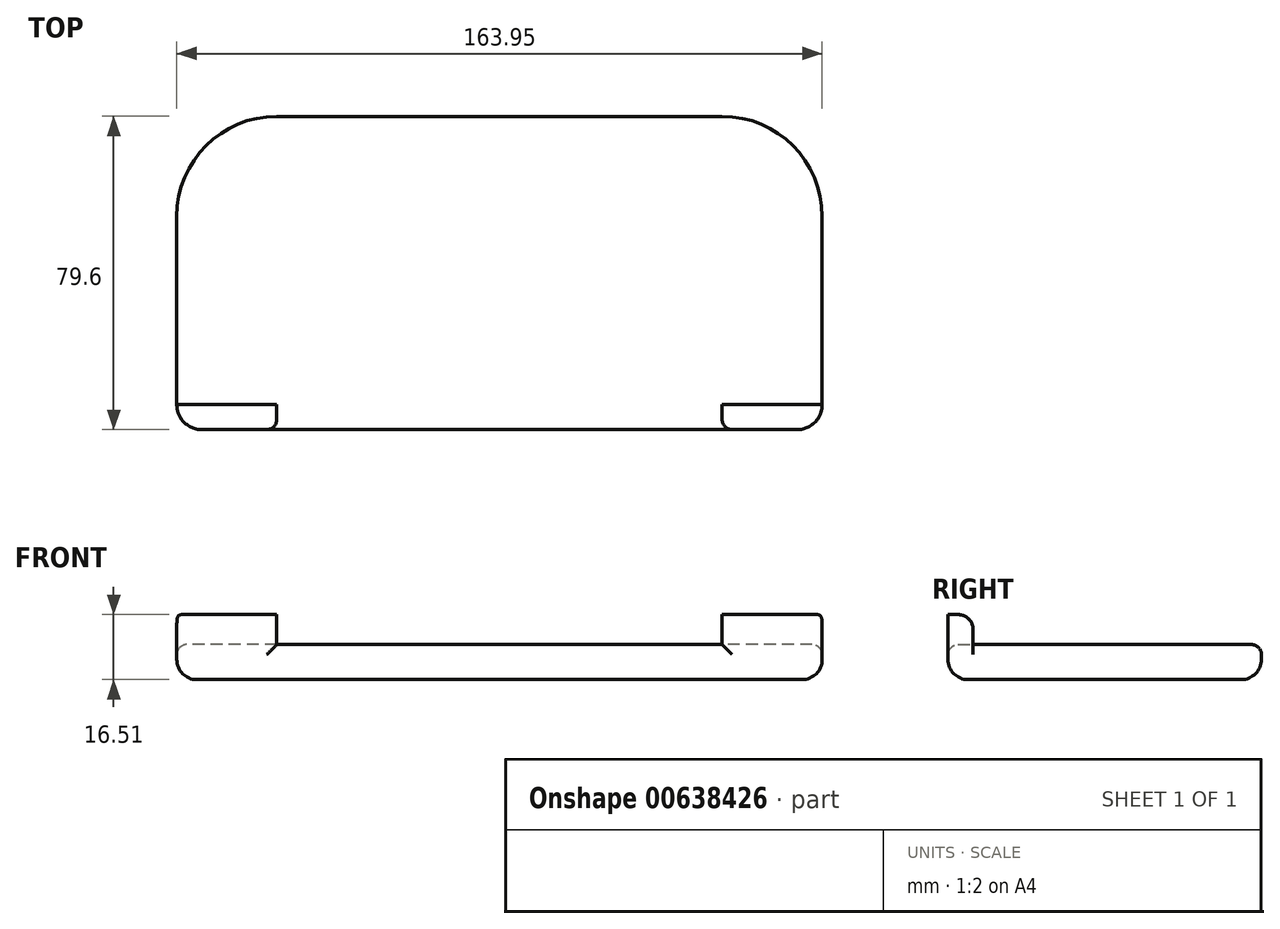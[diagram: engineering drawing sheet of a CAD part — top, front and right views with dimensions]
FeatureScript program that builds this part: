
annotation { "Feature Type Name" : "Feature", "Feature Type Description" : "" }
export const myFeature = defineFeature(function(context is Context, id is Id, definition is map)
    precondition{}
    {
        {
            var Q0;
            Q0=qCreatedBy(makeId("Top.planeOp"),FACE);
            var sketch = newSketch(context, id + "F0", { "sketchPlane" : qUnion([Q0])});
            skLineSegment(sketch, "E0.bottom", {"start": v(-90.4, 59.75) * mm, "end": v(22.75, 59.75) * mm});
            skLineSegment(sketch, "E0.top", {"start": v(-109.45, -19.85) * mm, "end": v(41.8, -19.85) * mm});
            skLineSegment(sketch, "E0.left", {"start": v(-115.8, 34.35) * mm, "end": v(-115.8, -13.5) * mm});
            skLineSegment(sketch, "E0.right", {"start": v(48.15, 34.35) * mm, "end": v(48.15, -13.5) * mm});
            skPoint(sketch, "E1.visualSharp", {"position": v(-115.8, 59.75) * mm});
            skArc(sketch, "E1.filletArc", {"start": v(-90.4, 59.75) * mm, "mid": v(-108.36, 52.3) * mm, "end": v(-115.8, 34.35) * mm});
            skPoint(sketch, "E2.visualSharp", {"position": v(48.15, 59.75) * mm});
            skArc(sketch, "E2.filletArc", {"start": v(48.15, 34.35) * mm, "mid": v(40.71, 52.3) * mm, "end": v(22.75, 59.75) * mm});
            skPoint(sketch, "E3.visualSharp", {"position": v(-115.8, -19.85) * mm});
            skArc(sketch, "E3.filletArc", {"start": v(-115.8, -13.5) * mm, "mid": v(-113.94, -18) * mm, "end": v(-109.45, -19.85) * mm});
            skPoint(sketch, "E4.visualSharp", {"position": v(48.15, -19.85) * mm});
            skArc(sketch, "E4.filletArc", {"start": v(41.8, -19.85) * mm, "mid": v(46.3, -18) * mm, "end": v(48.15, -13.5) * mm});
            skSolve(sketch);
        }
        {
            var Q0;
            Q0=makeQuery(id+"F0.imprint","IMPRINT",FACE,{"disambiguationData":[TD([[makeQuery(id+"F0.imprint","IMPRINT",EDGE,{"derivedFrom":sQuery(id+"F0.wireOp",EDGE,"E0.bottom")}),-1.0]])]});
            extrude(context, id + "F1", {"entities" : qUnion([Q0]), "depth" : 8.9 * mm, "offsetDistance" : 25.4 * mm});
        }
        {
            var Q0;
            Q0=makeQuery(id+"F1.opExtrude","CAP_FACE",FACE,{"disambiguationData":[OSD([sQuery(id+"F0.wireOp",EDGE,"E0.bottom"),sQuery(id+"F0.wireOp",EDGE,"E0.top"),sQuery(id+"F0.wireOp",EDGE,"E0.left"),sQuery(id+"F0.wireOp",EDGE,"E0.right"),sQuery(id+"F0.wireOp",EDGE,"E1.filletArc"),sQuery(id+"F0.wireOp",EDGE,"E2.filletArc"),sQuery(id+"F0.wireOp",EDGE,"E3.filletArc"),sQuery(id+"F0.wireOp",EDGE,"E4.filletArc")])],"isStart":false});
            var sketch = newSketch(context, id + "F2", { "sketchPlane" : qUnion([Q0])});
            skLineSegment(sketch, "E5.bottom", {"start": v(4.97, -5.3) * mm, "end": v(-71.23, -5.3) * mm});
            skLineSegment(sketch, "E5.top", {"start": v(4.97, 45.5) * mm, "end": v(-71.23, 45.5) * mm});
            skLineSegment(sketch, "E5.left", {"start": v(4.97, -5.3) * mm, "end": v(4.97, 45.5) * mm});
            skLineSegment(sketch, "E5.right", {"start": v(-71.23, -5.3) * mm, "end": v(-71.23, 45.5) * mm});
            skCircle(sketch, "E6", {"center": v(-93.22, 5.72) * mm, "radius": 3.26 * mm});
            skCircle(sketch, "E7.1.0", {"center": v(-85.48, 13.47) * mm, "radius": 3.26 * mm});
            skCircle(sketch, "E7.2.0", {"center": v(-93.22, 21.21) * mm, "radius": 3.26 * mm});
            skCircle(sketch, "E7.3.0", {"center": v(-100.97, 13.47) * mm, "radius": 3.26 * mm});
            skPoint(sketch, "E7.center", {"position": v(-93.22, 13.47) * mm});
            skCircle(sketch, "E8", {"center": v(29.1, 18.25) * mm, "radius": 6.35 * mm});
            skLineSegment(sketch, "E9.bottom", {"start": v(41.8, -20.12) * mm, "end": v(-109.45, -20.12) * mm});
            skLineSegment(sketch, "E9.top", {"start": v(48.15, -13.5) * mm, "end": v(-115.8, -13.5) * mm});
            skLineSegment(sketch, "E9.left", {"start": v(48.15, -13.77) * mm, "end": v(48.15, -13.5) * mm});
            skLineSegment(sketch, "E9.right", {"start": v(-115.8, -13.77) * mm, "end": v(-115.8, -13.5) * mm});
            skPoint(sketch, "E10.visualSharp", {"position": v(48.15, -20.12) * mm});
            skArc(sketch, "E10.filletArc", {"start": v(41.8, -20.12) * mm, "mid": v(46.3, -18.26) * mm, "end": v(48.15, -13.77) * mm});
            skPoint(sketch, "E11.visualSharp", {"position": v(-115.8, -20.12) * mm});
            skArc(sketch, "E11.filletArc", {"start": v(-115.8, -13.77) * mm, "mid": v(-113.94, -18.26) * mm, "end": v(-109.45, -20.12) * mm});
            skLineSegment(sketch, "E12", {"start": v(22.75, -19.85) * mm, "end": v(22.75, -13.5) * mm});
            skLineSegment(sketch, "E13", {"start": v(-90.4, -19.85) * mm, "end": v(-90.4, -13.5) * mm});
            skSolve(sketch);
        }
        {
            var Q0;
            {var subQ2=sQuery(id+"F2.wireOp",EDGE,"E12");Q0=makeQuery(id+"F2.imprint","IMPRINT",FACE,{"disambiguationData":[TD([[makeQuery(id+"F2.imprint","IMPRINT",EDGE,{"derivedFrom":subQ2}),-1.0]])]});}
            var Q1;
            {var subQ2=sQuery(id+"F2.wireOp",EDGE,"E13");Q1=makeQuery(id+"F2.imprint","IMPRINT",FACE,{"disambiguationData":[TD([[makeQuery(id+"F2.imprint","IMPRINT",EDGE,{"derivedFrom":subQ2}),1.0]])]});}
            extrude(context, id + "F3", {"entities" : qUnion([Q0, Q1]), "operationType" : NewBodyOperationType.ADD, "depth" : 7.62 * mm, "offsetDistance" : 25.4 * mm});
        }
        {
            var Q0;
            Q0=makeQuery(id+"F1.opExtrude","CAP_EDGE",EDGE,{"disambiguationData":[OSD([sQuery(id+"F0.wireOp",EDGE,"E2.filletArc")])],"isStart":false});
            fillet(context, id + "F4", {"entities" : qUnion([Q0]), "radius" : 2.54 * mm, "tangentPropagation" : true, "allowEdgeOverflow" : false});
        }
        {
            var Q0;
            Q0=makeQuery(id+"F1.opExtrude","CAP_EDGE",EDGE,{"disambiguationData":[OSD([sQuery(id+"F0.wireOp",EDGE,"E0.bottom")])],"isStart":true});
            fillet(context, id + "F5", {"entities" : qUnion([Q0]), "radius" : 5.08 * mm, "tangentPropagation" : true, "allowEdgeOverflow" : false});
        }
        {
            var Q0;
            {var subQ0=sQuery(id+"F2.wireOp",EDGE,"E9.top");Q0=makeQuery(id+"F3.opExtrude","CAP_EDGE",EDGE,{"disambiguationData":[OSD([subQ0]),TDD([makeQuery(id+"F2.imprint","IMPRINT",EDGE,{"disambiguationData":[TD([[makeQuery(id+"F2.imprint","INTERSECT",VERTEX,{"derivedFrom":[subQ0,sQuery(id+"F2.wireOp",EDGE,"E12")]}),1.0]])],"derivedFrom":subQ0})])],"isStart":false});}
            var Q1;
            {var subQ0=sQuery(id+"F2.wireOp",EDGE,"E9.top");Q1=makeQuery(id+"F3.opExtrude","CAP_EDGE",EDGE,{"disambiguationData":[OSD([subQ0]),TDD([makeQuery(id+"F2.imprint","IMPRINT",EDGE,{"disambiguationData":[TD([[makeQuery(id+"F2.imprint","INTERSECT",VERTEX,{"derivedFrom":[subQ0,sQuery(id+"F2.wireOp",EDGE,"E13")]}),-1.0]])],"derivedFrom":subQ0})])],"isStart":false});}
            fillet(context, id + "F6", {"entities" : qUnion([Q0, Q1]), "radius" : 3.8 * mm, "tangentPropagation" : true, "allowEdgeOverflow" : false});
        }
        {
            var Q0;
            Q0=makeQuery(id+"F3.opExtrude","SWEPT_EDGE",EDGE,{"disambiguationData":[OSD([sQuery(id+"F0.wireOp",EDGE,"E0.top"),sQuery(id+"F2.wireOp",EDGE,"E13")])]});
            var Q1;
            Q1=makeQuery(id+"F1.opExtrude","CAP_EDGE",EDGE,{"disambiguationData":[OSD([sQuery(id+"F0.wireOp",EDGE,"E0.top")])],"isStart":false});
            var Q2;
            Q2=makeQuery(id+"F3.opExtrude","SWEPT_EDGE",EDGE,{"disambiguationData":[OSD([sQuery(id+"F0.wireOp",EDGE,"E0.top"),sQuery(id+"F2.wireOp",EDGE,"E12")])]});
            fillet(context, id + "F7", {"entities" : qUnion([Q0, Q1, Q2]), "radius" : 2.54 * mm, "tangentPropagation" : true, "allowEdgeOverflow" : false});
        }
    });
